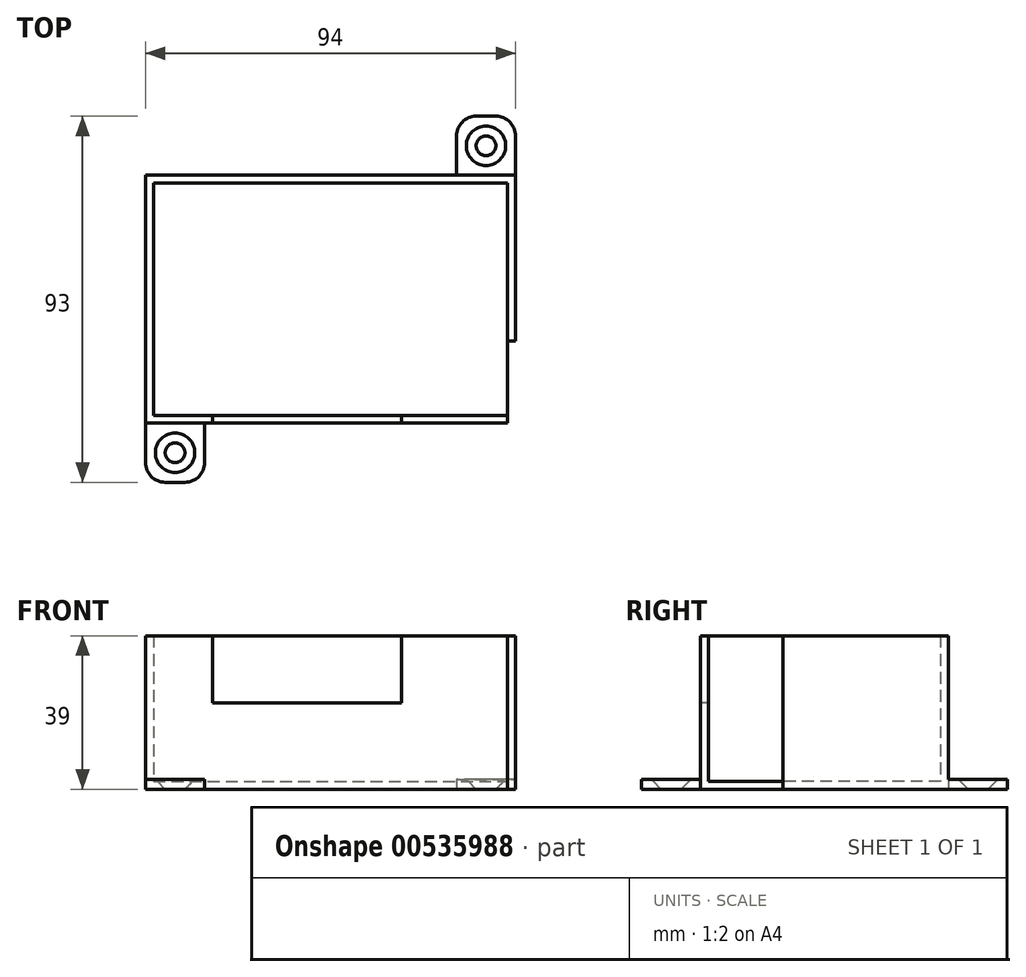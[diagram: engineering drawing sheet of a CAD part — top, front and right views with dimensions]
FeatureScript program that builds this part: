
annotation { "Feature Type Name" : "Feature", "Feature Type Description" : "" }
export const myFeature = defineFeature(function(context is Context, id is Id, definition is map)
    precondition{}
    {
        {
            var Q0;
            Q0=qCreatedBy(makeId("Top.planeOp"),FACE);
            var sketch = newSketch(context, id + "F0", { "sketchPlane" : qUnion([Q0])});
            skLineSegment(sketch, "E0.bottom", {"start": v(10.82, -7.1) * mm, "end": v(100.82, -7.1) * mm});
            skLineSegment(sketch, "E0.left", {"start": v(10.82, -7.1) * mm, "end": v(10.82, -66.1) * mm});
            skLineSegment(sketch, "E0.right", {"start": v(100.82, -7.1) * mm, "end": v(100.82, -68.26) * mm});
            skLineSegment(sketch, "E1.top", {"start": v(10.82, -5.1) * mm, "end": v(100.82, -5.1) * mm});
            skLineSegment(sketch, "E2.bottom", {"start": v(10.82, -66.1) * mm, "end": v(100.82, -66.1) * mm});
            skLineSegment(sketch, "E2.left", {"start": v(10.82, -66.1) * mm, "end": v(10.82, -66.1) * mm});
            skLineSegment(sketch, "E2.right", {"start": v(100.82, -68.26) * mm, "end": v(100.82, -66.1) * mm});
            skLineSegment(sketch, "E3.top", {"start": v(10.82, -68.1) * mm, "end": v(100.82, -68.1) * mm});
            skLineSegment(sketch, "E4.bottom", {"start": v(10.82, -5.1) * mm, "end": v(8.82, -5.1) * mm});
            skLineSegment(sketch, "E4.top", {"start": v(10.82, -68.1) * mm, "end": v(8.82, -68.1) * mm});
            skLineSegment(sketch, "E4.right", {"start": v(8.82, -5.1) * mm, "end": v(8.82, -68.1) * mm});
            skLineSegment(sketch, "E5.top", {"start": v(100.82, -68.1) * mm, "end": v(102.82, -68.1) * mm});
            skLineSegment(sketch, "E5.left", {"start": v(100.82, -7.1) * mm, "end": v(100.82, -66.1) * mm});
            skLineSegment(sketch, "E5.right", {"start": v(102.82, -7.5) * mm, "end": v(102.82, -68.1) * mm});
            skLineSegment(sketch, "E6.bottom", {"start": v(25.82, -66.1) * mm, "end": v(73.82, -66.1) * mm});
            skLineSegment(sketch, "E6.top", {"start": v(25.82, -68.1) * mm, "end": v(73.82, -68.1) * mm});
            skLineSegment(sketch, "E6.left", {"start": v(25.82, -66.1) * mm, "end": v(25.82, -68.1) * mm});
            skLineSegment(sketch, "E6.right", {"start": v(73.82, -66.1) * mm, "end": v(73.82, -68.1) * mm});
            skLineSegment(sketch, "E7.top", {"start": v(100.82, -47.24) * mm, "end": v(102.82, -47.24) * mm});
            skLineSegment(sketch, "E7.left", {"start": v(100.82, -68.26) * mm, "end": v(100.82, -47.24) * mm});
            skLineSegment(sketch, "E7.right", {"start": v(102.82, -68.26) * mm, "end": v(102.82, -47.24) * mm});
            skLineSegment(sketch, "E8.bottom", {"start": v(8.82, -68.1) * mm, "end": v(23.82, -68.1) * mm});
            skLineSegment(sketch, "E8.top", {"start": v(8.82, -83.1) * mm, "end": v(23.82, -83.1) * mm});
            skLineSegment(sketch, "E8.left", {"start": v(8.82, -68.1) * mm, "end": v(8.82, -83.1) * mm});
            skLineSegment(sketch, "E8.right", {"start": v(23.82, -68.1) * mm, "end": v(23.82, -83.1) * mm});
            skCircle(sketch, "E9", {"center": v(16.32, -75.6) * mm, "radius": 2 * mm});
            skLineSegment(sketch, "E10", {"start": v(102.82, -7.1) * mm, "end": v(102.82, -7.5) * mm});
            skLineSegment(sketch, "E11", {"start": v(100.82, -5.1) * mm, "end": v(102.82, -5.1) * mm});
            skLineSegment(sketch, "E12", {"start": v(102.82, -5.1) * mm, "end": v(102.82, -7.1) * mm});
            skLineSegment(sketch, "E13.bottom", {"start": v(102.82, -5.1) * mm, "end": v(87.82, -5.1) * mm});
            skLineSegment(sketch, "E13.top", {"start": v(102.82, 9.9) * mm, "end": v(87.82, 9.9) * mm});
            skLineSegment(sketch, "E13.left", {"start": v(102.82, -5.1) * mm, "end": v(102.82, 9.9) * mm});
            skLineSegment(sketch, "E13.right", {"start": v(87.82, -5.1) * mm, "end": v(87.82, 9.9) * mm});
            skCircle(sketch, "E14", {"center": v(95.32, 2.4) * mm, "radius": 2 * mm});
            skSolve(sketch);
        }
        {
            var Q0;
            {var subQ8=sQuery(id+"F0.wireOp",EDGE,"E0.bottom");Q0=makeQuery(id+"F0.imprint","IMPRINT",FACE,{"disambiguationData":[TD([[makeQuery(id+"F0.imprint","IMPRINT",EDGE,{"derivedFrom":subQ8}),1.0]])]});}
            var Q1;
            {var subQ5=sQuery(id+"F0.wireOp",EDGE,"E6.right");Q1=makeQuery(id+"F0.imprint","IMPRINT",FACE,{"disambiguationData":[TD([[makeQuery(id+"F0.imprint","IMPRINT",EDGE,{"derivedFrom":subQ5}),1.0]])]});}
            extrude(context, id + "F1", {"entities" : qUnion([Q0, Q1]), "depth" : 39 * mm, "offsetDistance" : 25 * mm});
        }
        {
            var Q0;
            {var subQ0=sQuery(id+"F0.wireOp",EDGE,"E6.left");Q0=makeQuery(id+"F0.imprint","IMPRINT",FACE,{"disambiguationData":[TD([[makeQuery(id+"F0.imprint","IMPRINT",EDGE,{"derivedFrom":subQ0}),1.0]])]});}
            extrude(context, id + "F2", {"entities" : qUnion([Q0]), "operationType" : NewBodyOperationType.ADD, "depth" : 22 * mm, "offsetDistance" : 25 * mm});
        }
        {
            var Q0;
            Q0=makeQuery(id+"F0.imprint","IMPRINT",FACE,{"disambiguationData":[TD([[makeQuery(id+"F0.imprint","IMPRINT",EDGE,{"derivedFrom":sQuery(id+"F0.wireOp",EDGE,"E0.bottom")}),-1.0]])]});
            extrude(context, id + "F3", {"entities" : qUnion([Q0]), "operationType" : NewBodyOperationType.ADD, "depth" : 2 * mm, "offsetDistance" : 25 * mm});
        }
        {
            var Q0;
            {var subQ0=sQuery(id+"F0.wireOp",EDGE,"E4.top");Q0=makeQuery(id+"F0.imprint","IMPRINT",FACE,{"disambiguationData":[TD([[makeQuery(id+"F0.imprint","IMPRINT",EDGE,{"derivedFrom":subQ0}),1.0]])]});}
            var Q1;
            {var subQ0=sQuery(id+"F0.wireOp",EDGE,"E11");Q1=makeQuery(id+"F0.imprint","IMPRINT",FACE,{"disambiguationData":[TD([[makeQuery(id+"F0.imprint","IMPRINT",EDGE,{"derivedFrom":subQ0}),1.0]])]});}
            extrude(context, id + "F4", {"entities" : qUnion([Q0, Q1]), "operationType" : NewBodyOperationType.ADD, "depth" : 2.5 * mm, "offsetDistance" : 25 * mm});
        }
        {
            var Q0;
            Q0=makeQuery(id+"F4.opExtrude","CAP_EDGE",EDGE,{"disambiguationData":[OSD([sQuery(id+"F0.wireOp",EDGE,"E9")])],"isStart":false});
            var Q1;
            Q1=makeQuery(id+"F4.opExtrude","CAP_EDGE",EDGE,{"disambiguationData":[OSD([sQuery(id+"F0.wireOp",EDGE,"E14")])],"isStart":false});
            chamfer(context, id + "F5", {"entities" : qUnion([Q0, Q1]), "width" : 3 * mm, "tangentPropagation" : true});
        }
        {
            var Q0;
            Q0=makeQuery(id+"F4.opExtrude","SWEPT_EDGE",EDGE,{"disambiguationData":[OSD([sQuery(id+"F0.wireOp",EDGE,"E13.top"),sQuery(id+"F0.wireOp",EDGE,"E13.left")])]});
            var Q1;
            Q1=makeQuery(id+"F4.opExtrude","SWEPT_EDGE",EDGE,{"disambiguationData":[OSD([sQuery(id+"F0.wireOp",EDGE,"E13.top"),sQuery(id+"F0.wireOp",EDGE,"E13.right")])]});
            var Q2;
            Q2=makeQuery(id+"F4.opExtrude","SWEPT_EDGE",EDGE,{"disambiguationData":[OSD([sQuery(id+"F0.wireOp",EDGE,"E8.top"),sQuery(id+"F0.wireOp",EDGE,"E8.left")])]});
            var Q3;
            Q3=makeQuery(id+"F4.opExtrude","SWEPT_EDGE",EDGE,{"disambiguationData":[OSD([sQuery(id+"F0.wireOp",EDGE,"E8.top"),sQuery(id+"F0.wireOp",EDGE,"E8.right")])]});
            fillet(context, id + "F6", {"entities" : qUnion([Q0, Q1, Q2, Q3]), "tangentPropagation" : true, "radius" : 5 * mm, "defaultsChanged" : false, "vertexSettings" : [], "allowEdgeOverflow" : false});
        }
    });
